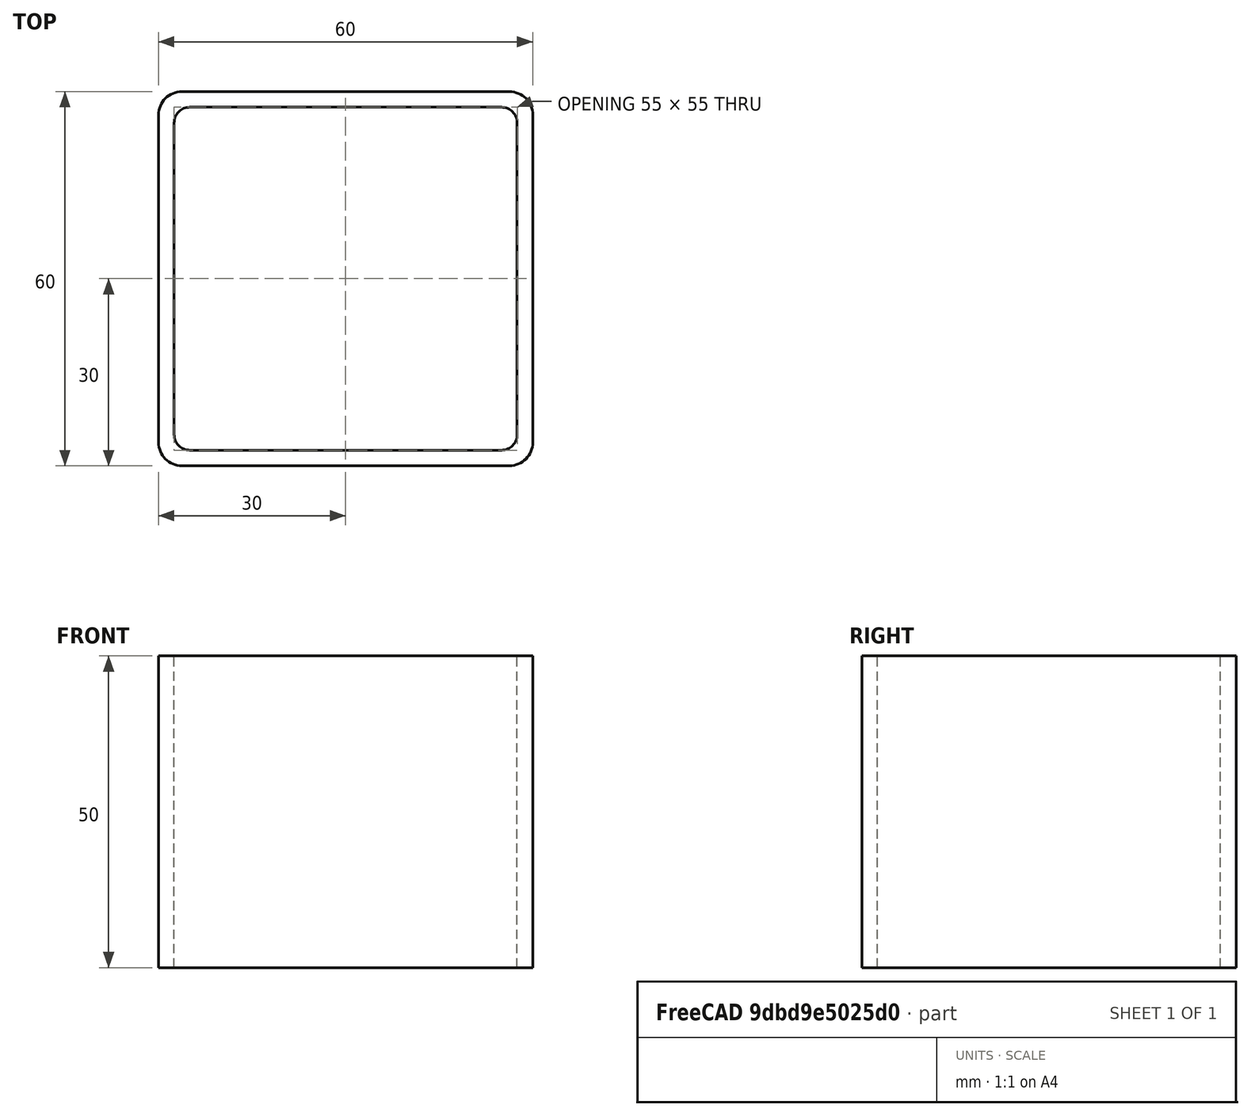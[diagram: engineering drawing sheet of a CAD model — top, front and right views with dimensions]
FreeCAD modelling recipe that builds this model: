
FCSTD DOCUMENT  (FreeCAD 0.15R4671 (Git))
Label: Square hollow section 60x60x2.5 EN10219 S235JRH
License: All rights reserved
LicenseURL: http://en.wikipedia.org/wiki/All_rights_reserved
objects: Sketcher::SketchObject×1, Part::Extrusion×1
note: 2 computed .brp shape members not serialized (recipe doc carries the construction recipe); baked Part::Feature solids carry a one-line shape summary decoded from their .brp

FEATURE [Sketcher::SketchObject] Sketch
  sketch-geometry (16):
    g0: LineSegment StartX=-25 StartY=27.5 StartZ=0 EndX=25 EndY=27.5 EndZ=0
    g1: LineSegment StartX=27.5 StartY=25 StartZ=0 EndX=27.5 EndY=-25 EndZ=0
    g2: LineSegment StartX=25 StartY=-27.5 StartZ=0 EndX=-25 EndY=-27.5 EndZ=0
    g3: LineSegment StartX=-27.5 StartY=-25 StartZ=0 EndX=-27.5 EndY=25 EndZ=0
    g4: LineSegment StartX=-26.25 StartY=30 StartZ=0 EndX=26.25 EndY=30 EndZ=0
    g5: LineSegment StartX=30 StartY=26.25 StartZ=0 EndX=30 EndY=-26.25 EndZ=0
    g6: LineSegment StartX=26.25 StartY=-30 StartZ=0 EndX=-26.25 EndY=-30 EndZ=0
    g7: LineSegment StartX=-30 StartY=-26.25 StartZ=0 EndX=-30 EndY=26.25 EndZ=0
    g8: ArcOfCircle CenterX=-25 CenterY=25 CenterZ=0 NormalX=0 NormalY=0 NormalZ=1 Radius=2.5 StartAngle=1.5708 EndAngle=3.14159
    g9: ArcOfCircle CenterX=25 CenterY=25 CenterZ=0 NormalX=0 NormalY=0 NormalZ=1 Radius=2.5 StartAngle=0 EndAngle=1.5708
    g10: ArcOfCircle CenterX=25 CenterY=-25 CenterZ=0 NormalX=0 NormalY=0 NormalZ=1 Radius=2.5 StartAngle=4.71239 EndAngle=6.28319
    g11: ArcOfCircle CenterX=-25 CenterY=-25 CenterZ=0 NormalX=0 NormalY=0 NormalZ=1 Radius=2.5 StartAngle=3.14159 EndAngle=4.71239
    g12: ArcOfCircle CenterX=26.25 CenterY=26.25 CenterZ=0 NormalX=0 NormalY=0 NormalZ=1 Radius=3.75 StartAngle=0 EndAngle=1.5708
    g13: ArcOfCircle CenterX=26.25 CenterY=-26.25 CenterZ=0 NormalX=0 NormalY=0 NormalZ=1 Radius=3.75 StartAngle=4.71239 EndAngle=6.28319
    g14: ArcOfCircle CenterX=-26.25 CenterY=-26.25 CenterZ=0 NormalX=0 NormalY=0 NormalZ=1 Radius=3.75 StartAngle=3.14159 EndAngle=4.71239
    g15: ArcOfCircle CenterX=-26.25 CenterY=26.25 CenterZ=0 NormalX=0 NormalY=0 NormalZ=1 Radius=3.75 StartAngle=1.5708 EndAngle=3.14159
  constraints (36):
    c: Horizontal(g2)
    c: Vertical(g3)
    c: Horizontal(g6)
    c: Vertical(g7)
    c: Tangent(g3,g8) = 1.5708
    c: Tangent(g0,g8) = 1.5708
    c: Tangent(g0,g9) = 1.5708
    c: Tangent(g1,g9) = 1.5708
    c: Tangent(g1,g10) = 1.5708
    c: Tangent(g2,g10) = 1.5708
    c: Tangent(g2,g11) = 1.5708
    c: Tangent(g3,g11) = 1.5708
    c: Tangent(g4,g12) = 1.5708
    c: Tangent(g5,g12) = 1.5708
    c: Tangent(g5,g13) = 1.5708
    c: Tangent(g6,g13) = 1.5708
    c: Tangent(g6,g14) = 1.5708
    c: Tangent(g7,g14) = 1.5708
    c: Tangent(g7,g15) = 1.5708
    c: Tangent(g4,g15) = 1.5708
    c: Equal(g9,g8)
    c: Equal(g9,g11)
    c: Equal(g9,g10)
    c: Equal(g12,g15)
    c: Equal(g12,g14)
    c: Equal(g12,g13)
    c: Symmetric(g4,g6,g-1)
    c: Symmetric(g7,g5,g-2)
    c: DistanceY(g4,g6) = -60
    c: DistanceX(g7,g5) = 60
    c: Symmetric(g3,g1,g-2)
    c: Symmetric(g0,g2,g-1)
    c: DistanceY(g0,g4) = 2.5
    c: DistanceX(g5,g1) = -2.5
    c: Radius(g9) = 2.5
    c: Radius(g12) = 3.75
FEATURE [Part::Extrusion] Extrude  label="Square hollow section 60x60x2.5 EN10219 S235JRH"
  Base = -> Sketch
  Dir = (0,0,50)
  Solid = true
